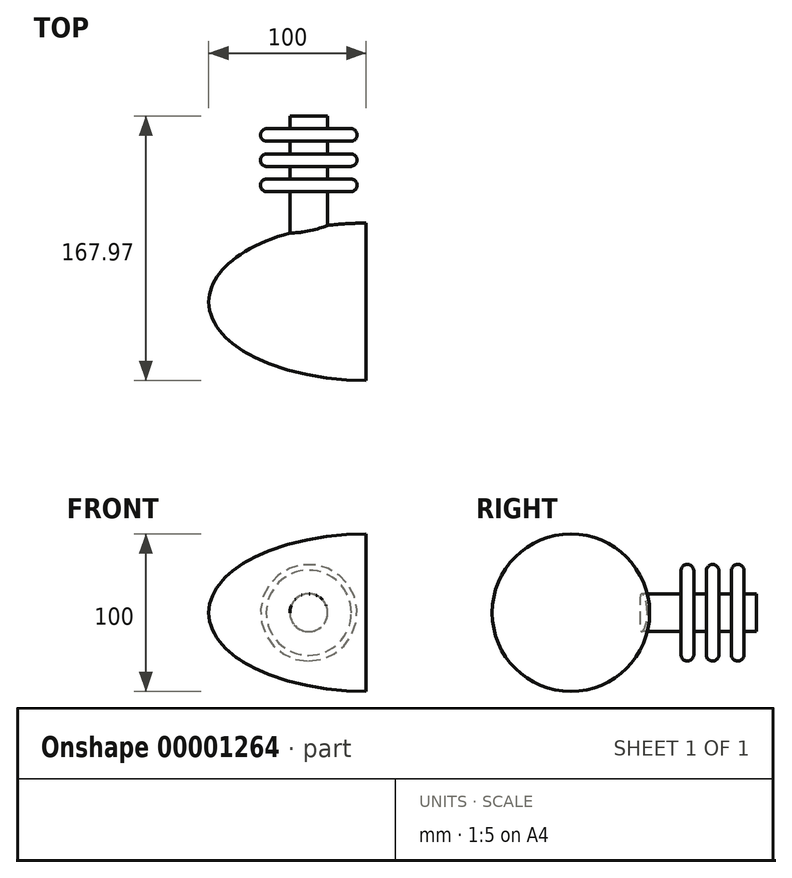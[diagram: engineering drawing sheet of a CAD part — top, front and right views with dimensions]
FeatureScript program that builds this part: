
annotation { "Feature Type Name" : "Feature", "Feature Type Description" : "" }
export const myFeature = defineFeature(function(context is Context, id is Id, definition is map)
    precondition{}
    {
        {
            var Q0;
            Q0=qCreatedBy(makeId("Top.planeOp"),FACE);
            var sketch = newSketch(context, id + "F0", { "sketchPlane" : qUnion([Q0])});
            skLineSegment(sketch, "E0", {"start": v(0, 0) * mm, "end": v(0, 50) * mm});
            skPoint(sketch, "E1.start.orphan", {"position": v(-100, 0) * mm});
            skEllipticalArc(sketch, "E2", {});
            skLineSegment(sketch, "E3", {"start": v(-100, 0) * mm, "end": v(0, 0) * mm});
            const initialGuessF0  = {"E2": [0, 0, -1, 0, 0.1, 0.05, 4.71238898038469, 0]};
            skSetInitialGuess(sketch, initialGuessF0);
            skSolve(sketch);
        }
        {
            var Q0;
            Q0=makeQuery(id+"F0.imprint","IMPRINT",FACE,{"disambiguationData":[TD([[makeQuery(id+"F0.imprint","IMPRINT",EDGE,{"derivedFrom":sQuery(id+"F0.wireOp",EDGE,"E0")}),1.0]])]});
            var Q1;
            Q1=sQuery(id+"F0.wireOp",EDGE,"E3");
            revolve(context, id + "F1", {"entities" : qUnion([Q0]), "axis" : qUnion([Q1]), "revolveType" : RevolveType.FULL});
        }
        {
            var Q0;
            Q0=qCreatedBy(makeId("Top.planeOp"),FACE);
            var sketch = newSketch(context, id + "F2", { "sketchPlane" : qUnion([Q0])});
            skLineSegment(sketch, "E4", {"start": v(-36.5, 0) * mm, "end": v(-36.5, 70) * mm});
            skLineSegment(sketch, "E5.bottom", {"start": v(-36.5, 0) * mm, "end": v(-48.5, 0) * mm});
            skLineSegment(sketch, "E5.right", {"start": v(-48.5, 0) * mm, "end": v(-48.5, 70) * mm});
            skLineSegment(sketch, "E6.bottom", {"start": v(-48.5, 70) * mm, "end": v(-63.2, 70) * mm});
            skLineSegment(sketch, "E6.right", {"start": v(-67.2, 77.72) * mm, "end": v(-67.06, 77.73) * mm});
            skLineSegment(sketch, "E7.right", {"start": v(-48.5, 77.99) * mm, "end": v(-48.5, 85.99) * mm});
            skPoint(sketch, "E8.visualSharp", {"position": v(-67.06, 77.73) * mm});
            skPoint(sketch, "E9.visualSharp", {"position": v(-172.7, 70) * mm});
            skArc(sketch, "E9.filletArc", {"start": v(-63.5, 77.99) * mm, "mid": v(-67.2, 73.85) * mm, "end": v(-63.2, 70) * mm});
            skLineSegment(sketch, "E10.0.1.0", {"start": v(-48.5, 93.98) * mm, "end": v(-48.5, 101.98) * mm});
            skLineSegment(sketch, "E10.0.1.1", {"start": v(-48.5, 85.99) * mm, "end": v(-63.2, 85.99) * mm});
            skArc(sketch, "E10.0.1.2", {"start": v(-63.5, 93.98) * mm, "mid": v(-67.2, 89.84) * mm, "end": v(-63.2, 85.99) * mm});
            skLineSegment(sketch, "E10.0.2.0", {"start": v(-48.5, 109.97) * mm, "end": v(-48.5, 117.97) * mm});
            skLineSegment(sketch, "E10.0.2.1", {"start": v(-48.5, 101.98) * mm, "end": v(-63.2, 101.98) * mm});
            skArc(sketch, "E10.0.2.2", {"start": v(-63.5, 109.97) * mm, "mid": v(-67.2, 105.83) * mm, "end": v(-63.2, 101.98) * mm});
            skLineSegment(sketch, "E10.direction1", {"start": v(0, 0) * mm, "end": v(25, 0) * mm, "construction": true});
            skLineSegment(sketch, "E10.direction2", {"start": v(0, 0) * mm, "end": v(0, 16) * mm, "construction": true});
            skPoint(sketch, "E11.orphan", {"position": v(-23.5, 101.98) * mm});
            skPoint(sketch, "E12.orphan", {"position": v(-23.5, 70) * mm});
            skLineSegment(sketch, "E13", {"start": v(-48.5, 117.97) * mm, "end": v(-36.5, 117.97) * mm});
            skPoint(sketch, "E7.left.start.orphan", {"position": v(-36.5, 77.73) * mm});
            skPoint(sketch, "E14.trimOffspring.end.orphan", {"position": v(-33.5, 93.97) * mm});
            skPoint(sketch, "E15.orphan", {"position": v(-33.5, 117.97) * mm});
            skLineSegment(sketch, "E16", {"start": v(-36.5, 70) * mm, "end": v(-36.5, 117.97) * mm});
            skLineSegment(sketch, "E17", {"start": v(-63.5, 93.98) * mm, "end": v(-48.5, 93.98) * mm});
            skLineSegment(sketch, "E18", {"start": v(-63.5, 109.97) * mm, "end": v(-48.5, 109.97) * mm});
            skLineSegment(sketch, "E19", {"start": v(-63.5, 77.99) * mm, "end": v(-48.5, 77.99) * mm});
            skLineSegment(sketch, "E20", {"start": v(-36.5, 117.97) * mm, "end": v(-36.5, 517.97) * mm});
            skSolve(sketch);
        }
        {
            var Q0;
            Q0=makeQuery(id+"F2.imprint","IMPRINT",FACE,{"disambiguationData":[TD([[makeQuery(id+"F2.imprint","IMPRINT",EDGE,{"derivedFrom":sQuery(id+"F2.wireOp",EDGE,"E5.bottom")}),-1.0]])]});
            var Q1;
            Q1=sQuery(id+"F2.wireOp",EDGE,"E4");
            revolve(context, id + "F3", {"operationType" : NewBodyOperationType.ADD, "entities" : qUnion([Q0]), "axis" : qUnion([Q1]), "revolveType" : RevolveType.FULL});
        }
        {
            var Q0;
            Q0=makeQuery(id+"F3.opRevolve","SWEPT_FACE",FACE,{"disambiguationData":[OSD([sQuery(id+"F2.wireOp",EDGE,"E13")])]});
            cPlane(context, id + "F4", {"entities" : qUnion([Q0]), "cplaneType" : CPlaneType.OFFSET, "offset" : 100 * mm, "width" : 150 * mm, "height" : 150 * mm});
        }
        {
            var Q0;
            Q0=qCreatedBy(id+"F4.planeOp",FACE);
            cPlane(context, id + "F5", {"entities" : qUnion([Q0]), "cplaneType" : CPlaneType.OFFSET, "offset" : 300 * mm, "width" : 150 * mm, "height" : 150 * mm});
        }
    });
